# Revit family: xxToilet-Elongated-American_Standard-Madera-345X_Series
name_source: partatom
category: Plumbing Fixtures
units: mm (PartAtom-declared; Revit-internal decimal feet)

## family parameters
Always vertical = No
Cut with Voids When Loaded = No
OmniClass Number = 23.45.05.21.11.11
OmniClass Title = Water Operated Water Closets
Part Type = Normal
Room Calculation Point = No
Round Connector Dimension = Use Diameter
Shared = Yes
Work Plane-Based = Yes

## types (4) — shared parameters
034783-0200A Bolt caps with retainers = Yes
047007-0070A Inlet Spud = Yes
10" Rough In = Yes
12" Rough In = No
5901.100 Seat- Heavy duty open front less cover = No
5901.100SS Seat- Heavy duty open front less cover with EverClean® = No
6047.121.002 Top Spud (1.28 gpf)- Manual = No
6047.161.002 Top Spud (1.6 gpf)- Manual = No
6065.121.002 Top Spud (1.28 gpf)- Sensor Operated Selectronic DC Power = No
6065.761.002 Top Spud (1.6/1.1 gpf Dual Flush)- Sensor Operated Selectronic DC Power = No
6065161.002 Top Spud (1.6 gpf)- Sensor Operated Selectronic® DC Power = No
6067.221.002 Back Spud (1.28 gpf)- Sensor Operated Selectronic AC Power = No
6067.261.002 Back Spud (1.6 gpf)- Sensor Operated Selectronic AC Power = No
ASME A112.19.2M for Vitreous China Fixtures = Yes
Assembly Code = D2010110
Bowl Shape = Elongated
CW Connection = Yes
CWFU = 10
Cold Water Connection Diameter = 1"
Cold Water Connection Height = 26 1/2"
Cold Water Connection Width = 4 3/4"
Default Elevation = 0"
Finish = Vitreous China-American Standard-020-White
Flush Rate = 1.1 gpf, 1.28 gpf or 1.6 gpf dual flush (4.2 Lpf to 6.0 Lpf)
HW Connection = No
Height = 15"
IAPMO Compliance = Environmental Product Declaration, CALGreen, CEC WaterSense Certified, EverClean® Surface, 
WaterSense
Installation Type = Floor Mounted
Length = 28 1/4"
Manufacturer = American Standard
Material = Vitreous China-American Standard-020-White
Price = Prices may vary. Please consult Manufacturer Representative for most up-to-date price list.
Product Documentation Link = https://americanstandard.box.com
Product Page URL = https://www.americanstandard-us.com
Recommended Working Pressure = Between 25 psi at valve when flushing and 80 psi static
Revised Date = 06/30/2022
Rough In Distance = 10"
URL = http://www.americanstandard-us.com
Vent Connection = No
WFU = 10
Warranty Information = 1 Year Limited Warranty
Waste Connection = Yes
Waste Connection Diameter = 2 1/8"
Width = 14"
zero-valued in all types: HWFU

## per-type parameters (varying)
| type | 3451.001 Elongated bowl only, top spud | 3452.001 Elongated bowl only, top spud with slotted rim for bedpan holding | 3453.001 Elongated bowl only, back spud | 3455.001 Elongated bowl only, back spud with slotted rim for bedpan holding | Bowl Rim | Cover | Description | Metal | Slotted rim for bedpan holding. | void |
| 3452.001.020 | No | Yes | No | No | No | No | Madera™ 1.1 – 1.6 gpf (4.2 – 6.0 Lpf) 15" Height Top Spud Elongated EverClean® Bowl With Bedpan Lugs | Yes | Yes | 1 1/8" |
| 3451.001.020 | Yes | No | No | No | Yes | No | Madera™ 1.1 – 1.6 gpf (4.2 – 6.0 Lpf) 15" Height Top Spud Elongated EverClean® Bowl | Yes | No | 1 1/8" |
| 3453.001.020 | No | No | Yes | No | Yes | Yes | Madera™ 1.1 – 1.6 gpf (4.2 – 6.0 Lpf) 15" Height Back Spud Elongated EverClean® Bowl | No | No | 0" |
| 3455.001.020 | No | No | No | Yes | No | Yes | Madera™ 1.1 – 1.6 gpf (4.2 – 6.0 Lpf) 15" Height Back Spud Elongated EverClean® Bowl With Bedpan Lugs | No | Yes | 0" |

note: column(s) folded — value = type name in every type: Model

## geometry (parser evidence)
native form markers: Sweep x2
no freeform markers — native parametric forms only
